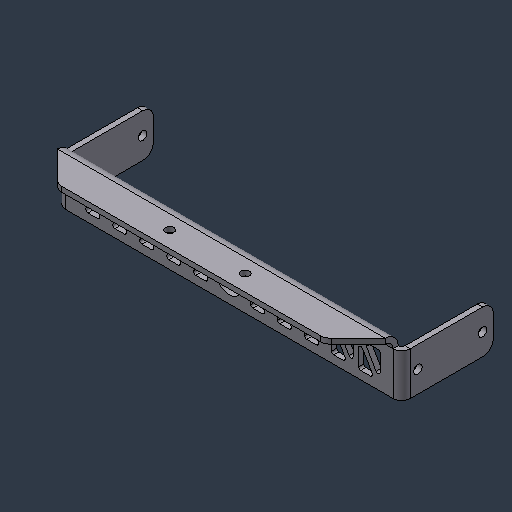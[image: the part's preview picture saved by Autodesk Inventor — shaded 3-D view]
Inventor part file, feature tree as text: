
AUTODESK INVENTOR PART (.ipt)
format: ipt  version: 2024.3 (Build 283343000, 343)  size: 470,016 bytes
history: native  units: mm (DEFAULTED — no unit token found)
features: sheet_metal_op x7, sketch x7, other x6, hole x3, chamfer x2, mirror x2, pattern_linear x1
ambient origin geometry x8: Origin, YZ Plane, XZ Plane, XY Plane, X Axis, Y Axis, Z Axis, Center Point
bodies: Solid1 (feature_tree)
feature tree (28):
  sheet_metal_op  "Face1"
  sheet_metal_op  "Flange2"
  sheet_metal_op  "Flange1"
  other  "Corner Chamfer1"
  chamfer  "Corner Round1"
  chamfer  "Corner Round2"
  pattern_linear  "Rectangular Pattern2"  Spacing1=25.4mm  [1 undecoded]
  mirror  "Mirror1"
  hole  "Hole3"  [1 undecoded]
  hole  "Hole4"  [1 undecoded]
  hole  "Hole5"  [1 undecoded]
  mirror  "Mirror2"
  sketch  "Sketch1"  dims[d0=203.2mm]
  other  "Plate1"
  sketch  "Sketch2"  dims[d1=25.4mm]
  other  "Plate2"
  sheet_metal_op  "Bend1"
  sheet_metal_op  "Corner1"
  sketch  "Sketch5"  dims[d2=3.048mm]
  sketch  "Sketch6"  dims[d3=3.048mm]
  sketch  "Sketch7"  dims[d4=1.524mm]
  sketch  "Sketch8"  dims[d5=6.096mm]
  other  "Plate3"
  sheet_metal_op  "Bend2"
  sheet_metal_op  "Corner2"
  sketch  "Sketch9"  dims[d6=4.572mm d7=25.4mm d8=90.0deg d9=4.572mm d10=12.192mm d11=3.048mm d12=4.572mm d13=17.78mm d14=6.35mm d15=45.0deg d16=6.35mm d36=12.7mm d37=15.875mm d38=60.0deg d39=12.7mm d40=3.048mm d41=0.0mm d42=1.27mm d43=50.0mm d45=15.875mm d46=12.0mm d48=16.0mm d49=19.05mm d50=9.525mm d51=6.35mm d52=14.3117mm d53=25.4mm d54=20.594885mm d55=44.45mm d56=9.525mm d57=5.1054mm d58=19.05mm d59=9.779mm d60=6.35mm d61=14.3117mm d62=25.4mm d63=20.594885mm d64=3.048mm d65=1.524mm d66=6.096mm d67=4.572mm d68=53.975mm d69=90.0deg d70=2.032mm d71=12.192mm d72=3.048mm d73=4.572mm d74=6.35mm d75=38.1mm d76=5.1054mm d77=9.652mm d78=9.779mm d79=6.35mm d80=14.3117mm d81=25.4mm d82=20.594885mm d44=20.594885mm d47=9.525mm]
  other  "Cut1"
  other  "Definition1"
note: 4 required parameter values undecoded (feature->parameter linkage not recoverable at this tier; creation-order binding heuristic only, values carry confidence <= 0.55)
